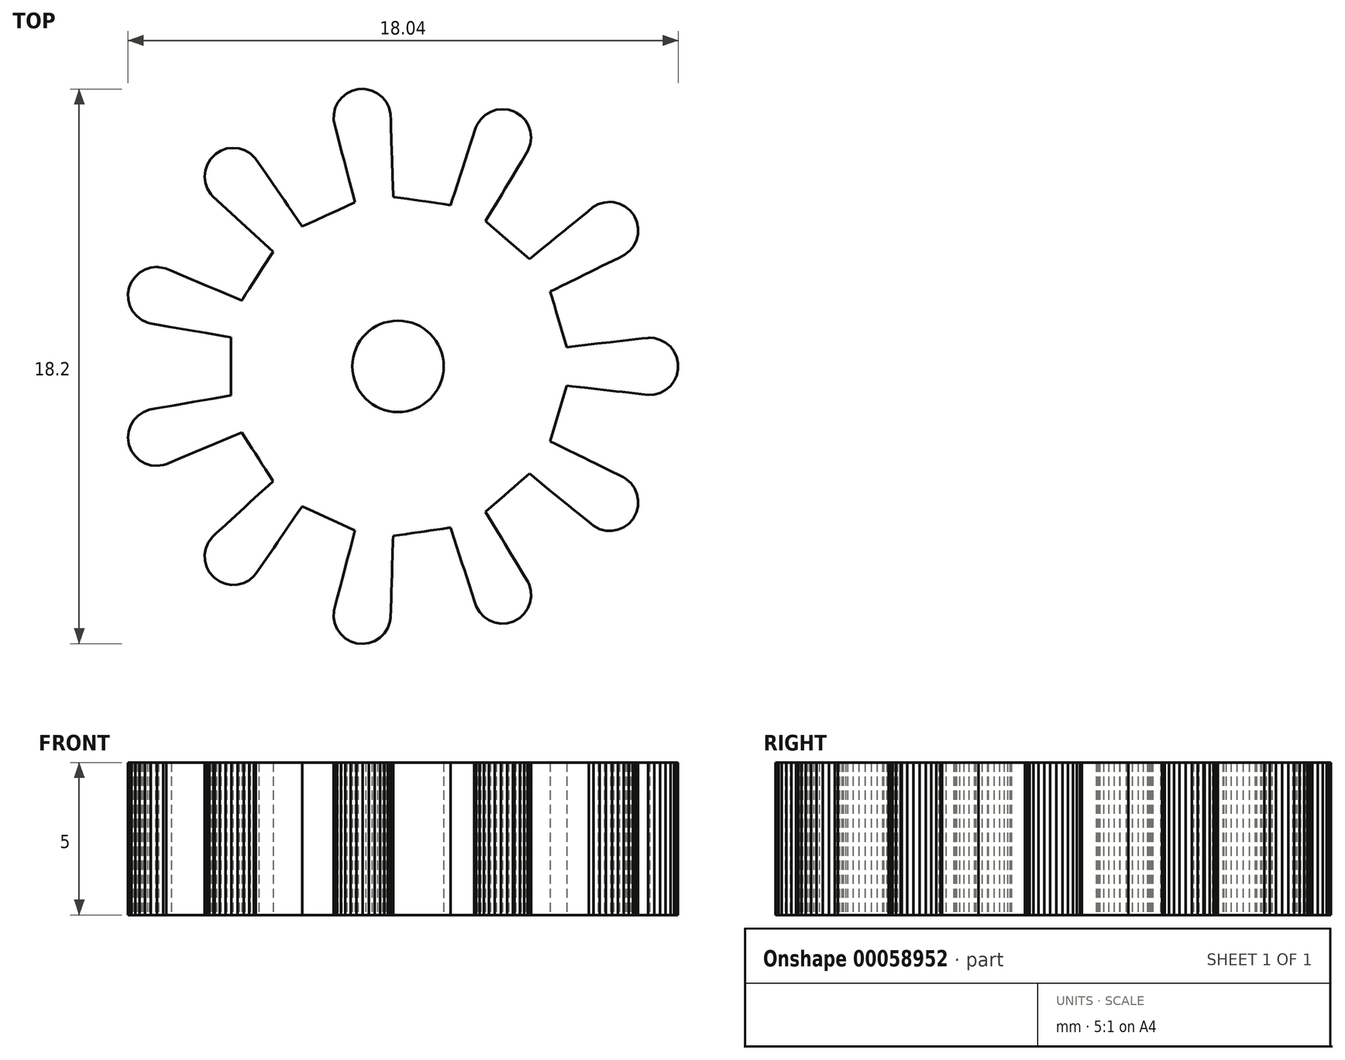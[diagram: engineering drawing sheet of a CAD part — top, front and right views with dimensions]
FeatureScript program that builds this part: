
annotation { "Feature Type Name" : "Feature", "Feature Type Description" : "" }
export const myFeature = defineFeature(function(context is Context, id is Id, definition is map)
    precondition{}
    {
        {
            var Q0;
            Q0=qCreatedBy(makeId("Top.planeOp"),FACE);
            var sketch = newSketch(context, id + "F0", { "sketchPlane" : qUnion([Q0])});
            skLineSegment(sketch, "E0", {"start": v(4.1, -0.63) * mm, "end": v(4.27, -0.65) * mm});
            skLineSegment(sketch, "E1", {"start": v(4.27, -0.65) * mm, "end": v(4.48, -0.68) * mm});
            skLineSegment(sketch, "E2", {"start": v(4.48, -0.68) * mm, "end": v(4.68, -0.7) * mm});
            skLineSegment(sketch, "E3", {"start": v(4.68, -0.7) * mm, "end": v(4.9, -0.72) * mm});
            skLineSegment(sketch, "E4", {"start": v(4.9, -0.72) * mm, "end": v(5.1, -0.75) * mm});
            skLineSegment(sketch, "E5", {"start": v(5.1, -0.75) * mm, "end": v(5.3, -0.77) * mm});
            skLineSegment(sketch, "E6", {"start": v(5.3, -0.77) * mm, "end": v(5.51, -0.8) * mm});
            skLineSegment(sketch, "E7", {"start": v(5.51, -0.8) * mm, "end": v(5.72, -0.82) * mm});
            skLineSegment(sketch, "E8", {"start": v(5.72, -0.82) * mm, "end": v(5.93, -0.84) * mm});
            skLineSegment(sketch, "E9", {"start": v(5.93, -0.84) * mm, "end": v(6.14, -0.86) * mm});
            skLineSegment(sketch, "E10", {"start": v(6.14, -0.86) * mm, "end": v(6.34, -0.89) * mm});
            skLineSegment(sketch, "E11", {"start": v(6.34, -0.89) * mm, "end": v(6.55, -0.91) * mm});
            skLineSegment(sketch, "E12", {"start": v(6.55, -0.91) * mm, "end": v(6.76, -0.94) * mm});
            skLineSegment(sketch, "E13", {"start": v(6.76, -0.94) * mm, "end": v(6.96, -0.93) * mm});
            skLineSegment(sketch, "E14", {"start": v(6.96, -0.93) * mm, "end": v(7.16, -0.87) * mm});
            skLineSegment(sketch, "E15", {"start": v(7.16, -0.87) * mm, "end": v(7.34, -0.78) * mm});
            skLineSegment(sketch, "E16", {"start": v(7.34, -0.78) * mm, "end": v(7.5, -0.65) * mm});
            skLineSegment(sketch, "E17", {"start": v(7.5, -0.65) * mm, "end": v(7.62, -0.48) * mm});
            skLineSegment(sketch, "E18", {"start": v(7.62, -0.48) * mm, "end": v(7.7, -0.3) * mm});
            skLineSegment(sketch, "E19", {"start": v(7.7, -0.3) * mm, "end": v(7.75, -0.1) * mm});
            skLineSegment(sketch, "E20", {"start": v(7.75, -0.1) * mm, "end": v(7.75, 0.1) * mm});
            skLineSegment(sketch, "E21", {"start": v(7.75, 0.1) * mm, "end": v(7.7, 0.3) * mm});
            skLineSegment(sketch, "E22", {"start": v(7.7, 0.3) * mm, "end": v(7.62, 0.48) * mm});
            skLineSegment(sketch, "E23", {"start": v(7.62, 0.48) * mm, "end": v(7.5, 0.65) * mm});
            skLineSegment(sketch, "E24", {"start": v(7.5, 0.65) * mm, "end": v(7.34, 0.78) * mm});
            skLineSegment(sketch, "E25", {"start": v(7.34, 0.78) * mm, "end": v(7.16, 0.87) * mm});
            skLineSegment(sketch, "E26", {"start": v(7.16, 0.87) * mm, "end": v(6.96, 0.93) * mm});
            skLineSegment(sketch, "E27", {"start": v(6.96, 0.93) * mm, "end": v(6.81, 0.94) * mm});
            skLineSegment(sketch, "E28", {"start": v(6.81, 0.94) * mm, "end": v(6.76, 0.94) * mm});
            skLineSegment(sketch, "E29", {"start": v(6.76, 0.94) * mm, "end": v(6.55, 0.91) * mm});
            skLineSegment(sketch, "E30", {"start": v(6.55, 0.91) * mm, "end": v(6.35, 0.89) * mm});
            skLineSegment(sketch, "E31", {"start": v(6.35, 0.89) * mm, "end": v(6.14, 0.86) * mm});
            skLineSegment(sketch, "E32", {"start": v(6.14, 0.86) * mm, "end": v(5.93, 0.84) * mm});
            skLineSegment(sketch, "E33", {"start": v(5.93, 0.84) * mm, "end": v(5.73, 0.82) * mm});
            skLineSegment(sketch, "E34", {"start": v(5.73, 0.82) * mm, "end": v(5.51, 0.8) * mm});
            skLineSegment(sketch, "E35", {"start": v(5.51, 0.8) * mm, "end": v(5.3, 0.77) * mm});
            skLineSegment(sketch, "E36", {"start": v(5.3, 0.77) * mm, "end": v(5.1, 0.75) * mm});
            skLineSegment(sketch, "E37", {"start": v(5.1, 0.75) * mm, "end": v(4.9, 0.72) * mm});
            skLineSegment(sketch, "E38", {"start": v(4.9, 0.72) * mm, "end": v(4.69, 0.7) * mm});
            skLineSegment(sketch, "E39", {"start": v(4.69, 0.7) * mm, "end": v(4.48, 0.68) * mm});
            skLineSegment(sketch, "E40", {"start": v(4.48, 0.68) * mm, "end": v(4.27, 0.65) * mm});
            skLineSegment(sketch, "E41", {"start": v(4.27, 0.65) * mm, "end": v(4.1, 0.63) * mm});
            skLineSegment(sketch, "E42", {"start": v(4.1, 0.63) * mm, "end": v(4.03, 0.83) * mm});
            skLineSegment(sketch, "E43", {"start": v(4.03, 0.83) * mm, "end": v(3.98, 1.03) * mm});
            skLineSegment(sketch, "E44", {"start": v(3.98, 1.03) * mm, "end": v(3.92, 1.23) * mm});
            skLineSegment(sketch, "E45", {"start": v(3.92, 1.23) * mm, "end": v(3.86, 1.42) * mm});
            skLineSegment(sketch, "E46", {"start": v(3.86, 1.42) * mm, "end": v(3.8, 1.62) * mm});
            skLineSegment(sketch, "E47", {"start": v(3.8, 1.62) * mm, "end": v(3.74, 1.82) * mm});
            skLineSegment(sketch, "E48", {"start": v(3.74, 1.82) * mm, "end": v(3.68, 2.02) * mm});
            skLineSegment(sketch, "E49", {"start": v(3.68, 2.02) * mm, "end": v(3.63, 2.22) * mm});
            skLineSegment(sketch, "E50", {"start": v(3.63, 2.22) * mm, "end": v(3.57, 2.41) * mm});
            skLineSegment(sketch, "E51", {"start": v(3.57, 2.41) * mm, "end": v(3.56, 2.46) * mm});
            skLineSegment(sketch, "E52", {"start": v(3.56, 2.46) * mm, "end": v(3.74, 2.55) * mm});
            skLineSegment(sketch, "E53", {"start": v(3.74, 2.55) * mm, "end": v(3.93, 2.64) * mm});
            skLineSegment(sketch, "E54", {"start": v(3.93, 2.64) * mm, "end": v(4.12, 2.73) * mm});
            skLineSegment(sketch, "E55", {"start": v(4.12, 2.73) * mm, "end": v(4.3, 2.83) * mm});
            skLineSegment(sketch, "E56", {"start": v(4.3, 2.83) * mm, "end": v(4.49, 2.92) * mm});
            skLineSegment(sketch, "E57", {"start": v(4.49, 2.92) * mm, "end": v(4.68, 3.01) * mm});
            skLineSegment(sketch, "E58", {"start": v(4.68, 3.01) * mm, "end": v(4.87, 3.1) * mm});
            skLineSegment(sketch, "E59", {"start": v(4.87, 3.1) * mm, "end": v(5.05, 3.2) * mm});
            skLineSegment(sketch, "E60", {"start": v(5.05, 3.2) * mm, "end": v(5.24, 3.29) * mm});
            skLineSegment(sketch, "E61", {"start": v(5.24, 3.29) * mm, "end": v(5.43, 3.38) * mm});
            skLineSegment(sketch, "E62", {"start": v(5.43, 3.38) * mm, "end": v(5.61, 3.47) * mm});
            skLineSegment(sketch, "E63", {"start": v(5.61, 3.47) * mm, "end": v(5.8, 3.57) * mm});
            skLineSegment(sketch, "E64", {"start": v(5.8, 3.57) * mm, "end": v(5.99, 3.66) * mm});
            skLineSegment(sketch, "E65", {"start": v(5.99, 3.66) * mm, "end": v(6.17, 3.8) * mm});
            skLineSegment(sketch, "E66", {"start": v(6.17, 3.8) * mm, "end": v(6.3, 3.96) * mm});
            skLineSegment(sketch, "E67", {"start": v(6.3, 3.96) * mm, "end": v(6.38, 4.14) * mm});
            skLineSegment(sketch, "E68", {"start": v(6.38, 4.14) * mm, "end": v(6.43, 4.33) * mm});
            skLineSegment(sketch, "E69", {"start": v(6.43, 4.33) * mm, "end": v(6.44, 4.54) * mm});
            skLineSegment(sketch, "E70", {"start": v(6.44, 4.54) * mm, "end": v(6.4, 4.74) * mm});
            skLineSegment(sketch, "E71", {"start": v(6.4, 4.74) * mm, "end": v(6.32, 4.92) * mm});
            skLineSegment(sketch, "E72", {"start": v(6.32, 4.92) * mm, "end": v(6.3, 4.97) * mm});
            skLineSegment(sketch, "E73", {"start": v(6.3, 4.97) * mm, "end": v(6.16, 5.13) * mm});
            skLineSegment(sketch, "E74", {"start": v(6.16, 5.13) * mm, "end": v(6, 5.25) * mm});
            skLineSegment(sketch, "E75", {"start": v(6, 5.25) * mm, "end": v(5.82, 5.34) * mm});
            skLineSegment(sketch, "E76", {"start": v(5.82, 5.34) * mm, "end": v(5.63, 5.39) * mm});
            skLineSegment(sketch, "E77", {"start": v(5.63, 5.39) * mm, "end": v(5.53, 5.4) * mm});
            skLineSegment(sketch, "E78", {"start": v(5.53, 5.4) * mm, "end": v(5.32, 5.38) * mm});
            skLineSegment(sketch, "E79", {"start": v(5.32, 5.38) * mm, "end": v(5.13, 5.32) * mm});
            skLineSegment(sketch, "E80", {"start": v(5.13, 5.32) * mm, "end": v(4.95, 5.22) * mm});
            skLineSegment(sketch, "E81", {"start": v(4.95, 5.22) * mm, "end": v(4.8, 5.09) * mm});
            skLineSegment(sketch, "E82", {"start": v(4.8, 5.09) * mm, "end": v(4.63, 4.96) * mm});
            skLineSegment(sketch, "E83", {"start": v(4.63, 4.96) * mm, "end": v(4.47, 4.82) * mm});
            skLineSegment(sketch, "E84", {"start": v(4.47, 4.82) * mm, "end": v(4.3, 4.7) * mm});
            skLineSegment(sketch, "E85", {"start": v(4.3, 4.7) * mm, "end": v(4.15, 4.56) * mm});
            skLineSegment(sketch, "E86", {"start": v(4.15, 4.56) * mm, "end": v(3.98, 4.43) * mm});
            skLineSegment(sketch, "E87", {"start": v(3.98, 4.43) * mm, "end": v(3.82, 4.3) * mm});
            skLineSegment(sketch, "E88", {"start": v(3.82, 4.3) * mm, "end": v(3.66, 4.16) * mm});
            skLineSegment(sketch, "E89", {"start": v(3.66, 4.16) * mm, "end": v(3.5, 4.03) * mm});
            skLineSegment(sketch, "E90", {"start": v(3.5, 4.03) * mm, "end": v(3.34, 3.9) * mm});
            skLineSegment(sketch, "E91", {"start": v(3.34, 3.9) * mm, "end": v(3.18, 3.77) * mm});
            skLineSegment(sketch, "E92", {"start": v(3.18, 3.77) * mm, "end": v(3.01, 3.63) * mm});
            skLineSegment(sketch, "E93", {"start": v(3.01, 3.63) * mm, "end": v(2.87, 3.52) * mm});
            skLineSegment(sketch, "E94", {"start": v(2.87, 3.52) * mm, "end": v(2.72, 3.66) * mm});
            skLineSegment(sketch, "E95", {"start": v(2.72, 3.66) * mm, "end": v(2.56, 3.8) * mm});
            skLineSegment(sketch, "E96", {"start": v(2.56, 3.8) * mm, "end": v(2.4, 3.93) * mm});
            skLineSegment(sketch, "E97", {"start": v(2.4, 3.93) * mm, "end": v(2.25, 4.06) * mm});
            skLineSegment(sketch, "E98", {"start": v(2.25, 4.06) * mm, "end": v(2.1, 4.2) * mm});
            skLineSegment(sketch, "E99", {"start": v(2.1, 4.2) * mm, "end": v(1.94, 4.33) * mm});
            skLineSegment(sketch, "E100", {"start": v(1.94, 4.33) * mm, "end": v(1.78, 4.47) * mm});
            skLineSegment(sketch, "E101", {"start": v(1.78, 4.47) * mm, "end": v(1.62, 4.6) * mm});
            skLineSegment(sketch, "E102", {"start": v(1.62, 4.6) * mm, "end": v(1.47, 4.74) * mm});
            skLineSegment(sketch, "E103", {"start": v(1.47, 4.74) * mm, "end": v(1.43, 4.77) * mm});
            skLineSegment(sketch, "E104", {"start": v(1.43, 4.77) * mm, "end": v(1.54, 4.94) * mm});
            skLineSegment(sketch, "E105", {"start": v(1.54, 4.94) * mm, "end": v(1.65, 5.12) * mm});
            skLineSegment(sketch, "E106", {"start": v(1.65, 5.12) * mm, "end": v(1.76, 5.3) * mm});
            skLineSegment(sketch, "E107", {"start": v(1.76, 5.3) * mm, "end": v(1.86, 5.48) * mm});
            skLineSegment(sketch, "E108", {"start": v(1.86, 5.48) * mm, "end": v(1.97, 5.66) * mm});
            skLineSegment(sketch, "E109", {"start": v(1.97, 5.66) * mm, "end": v(2.08, 5.84) * mm});
            skLineSegment(sketch, "E110", {"start": v(2.08, 5.84) * mm, "end": v(2.19, 6.02) * mm});
            skLineSegment(sketch, "E111", {"start": v(2.19, 6.02) * mm, "end": v(2.3, 6.2) * mm});
            skLineSegment(sketch, "E112", {"start": v(2.3, 6.2) * mm, "end": v(2.4, 6.38) * mm});
            skLineSegment(sketch, "E113", {"start": v(2.4, 6.38) * mm, "end": v(2.51, 6.55) * mm});
            skLineSegment(sketch, "E114", {"start": v(2.51, 6.55) * mm, "end": v(2.62, 6.73) * mm});
            skLineSegment(sketch, "E115", {"start": v(2.62, 6.73) * mm, "end": v(2.73, 6.91) * mm});
            skLineSegment(sketch, "E116", {"start": v(2.73, 6.91) * mm, "end": v(2.83, 7.1) * mm});
            skLineSegment(sketch, "E117", {"start": v(2.83, 7.1) * mm, "end": v(2.9, 7.3) * mm});
            skLineSegment(sketch, "E118", {"start": v(2.9, 7.3) * mm, "end": v(2.93, 7.5) * mm});
            skLineSegment(sketch, "E119", {"start": v(2.93, 7.5) * mm, "end": v(2.9, 7.7) * mm});
            skLineSegment(sketch, "E120", {"start": v(2.9, 7.7) * mm, "end": v(2.84, 7.9) * mm});
            skLineSegment(sketch, "E121", {"start": v(2.84, 7.9) * mm, "end": v(2.73, 8.07) * mm});
            skLineSegment(sketch, "E122", {"start": v(2.73, 8.07) * mm, "end": v(2.6, 8.22) * mm});
            skLineSegment(sketch, "E123", {"start": v(2.6, 8.22) * mm, "end": v(2.43, 8.33) * mm});
            skLineSegment(sketch, "E124", {"start": v(2.43, 8.33) * mm, "end": v(2.38, 8.36) * mm});
            skLineSegment(sketch, "E125", {"start": v(2.38, 8.36) * mm, "end": v(2.19, 8.42) * mm});
            skLineSegment(sketch, "E126", {"start": v(2.19, 8.42) * mm, "end": v(1.99, 8.44) * mm});
            skLineSegment(sketch, "E127", {"start": v(1.99, 8.44) * mm, "end": v(1.78, 8.42) * mm});
            skLineSegment(sketch, "E128", {"start": v(1.78, 8.42) * mm, "end": v(1.6, 8.35) * mm});
            skLineSegment(sketch, "E129", {"start": v(1.6, 8.35) * mm, "end": v(1.42, 8.25) * mm});
            skLineSegment(sketch, "E130", {"start": v(1.42, 8.25) * mm, "end": v(1.27, 8.1) * mm});
            skLineSegment(sketch, "E131", {"start": v(1.27, 8.1) * mm, "end": v(1.16, 7.94) * mm});
            skLineSegment(sketch, "E132", {"start": v(1.16, 7.94) * mm, "end": v(1.12, 7.84) * mm});
            skLineSegment(sketch, "E133", {"start": v(1.12, 7.84) * mm, "end": v(1.05, 7.65) * mm});
            skLineSegment(sketch, "E134", {"start": v(1.05, 7.65) * mm, "end": v(0.99, 7.45) * mm});
            skLineSegment(sketch, "E135", {"start": v(0.99, 7.45) * mm, "end": v(0.92, 7.25) * mm});
            skLineSegment(sketch, "E136", {"start": v(0.92, 7.25) * mm, "end": v(0.86, 7.05) * mm});
            skLineSegment(sketch, "E137", {"start": v(0.86, 7.05) * mm, "end": v(0.8, 6.86) * mm});
            skLineSegment(sketch, "E138", {"start": v(0.8, 6.86) * mm, "end": v(0.73, 6.65) * mm});
            skLineSegment(sketch, "E139", {"start": v(0.73, 6.65) * mm, "end": v(0.67, 6.46) * mm});
            skLineSegment(sketch, "E140", {"start": v(0.67, 6.46) * mm, "end": v(0.6, 6.26) * mm});
            skLineSegment(sketch, "E141", {"start": v(0.6, 6.26) * mm, "end": v(0.54, 6.06) * mm});
            skLineSegment(sketch, "E142", {"start": v(0.54, 6.06) * mm, "end": v(0.47, 5.86) * mm});
            skLineSegment(sketch, "E143", {"start": v(0.47, 5.86) * mm, "end": v(0.4, 5.66) * mm});
            skLineSegment(sketch, "E144", {"start": v(0.4, 5.66) * mm, "end": v(0.34, 5.46) * mm});
            skLineSegment(sketch, "E145", {"start": v(0.34, 5.46) * mm, "end": v(0.29, 5.3) * mm});
            skLineSegment(sketch, "E146", {"start": v(0.29, 5.3) * mm, "end": v(0.08, 5.32) * mm});
            skLineSegment(sketch, "E147", {"start": v(0.08, 5.32) * mm, "end": v(-0.12, 5.35) * mm});
            skLineSegment(sketch, "E148", {"start": v(-0.12, 5.35) * mm, "end": v(-0.33, 5.38) * mm});
            skLineSegment(sketch, "E149", {"start": v(-0.33, 5.38) * mm, "end": v(-0.53, 5.4) * mm});
            skLineSegment(sketch, "E150", {"start": v(-0.53, 5.4) * mm, "end": v(-0.74, 5.44) * mm});
            skLineSegment(sketch, "E151", {"start": v(-0.74, 5.44) * mm, "end": v(-0.94, 5.47) * mm});
            skLineSegment(sketch, "E152", {"start": v(-0.94, 5.47) * mm, "end": v(-1.15, 5.5) * mm});
            skLineSegment(sketch, "E153", {"start": v(-1.15, 5.5) * mm, "end": v(-1.35, 5.53) * mm});
            skLineSegment(sketch, "E154", {"start": v(-1.35, 5.53) * mm, "end": v(-1.55, 5.56) * mm});
            skLineSegment(sketch, "E155", {"start": v(-1.55, 5.56) * mm, "end": v(-1.6, 5.56) * mm});
            skLineSegment(sketch, "E156", {"start": v(-1.6, 5.56) * mm, "end": v(-1.6, 5.77) * mm});
            skLineSegment(sketch, "E157", {"start": v(-1.6, 5.77) * mm, "end": v(-1.61, 5.98) * mm});
            skLineSegment(sketch, "E158", {"start": v(-1.61, 5.98) * mm, "end": v(-1.62, 6.19) * mm});
            skLineSegment(sketch, "E159", {"start": v(-1.62, 6.19) * mm, "end": v(-1.62, 6.4) * mm});
            skLineSegment(sketch, "E160", {"start": v(-1.62, 6.4) * mm, "end": v(-1.63, 6.6) * mm});
            skLineSegment(sketch, "E161", {"start": v(-1.63, 6.6) * mm, "end": v(-1.64, 6.82) * mm});
            skLineSegment(sketch, "E162", {"start": v(-1.64, 6.82) * mm, "end": v(-1.64, 7.02) * mm});
            skLineSegment(sketch, "E163", {"start": v(-1.64, 7.02) * mm, "end": v(-1.65, 7.23) * mm});
            skLineSegment(sketch, "E164", {"start": v(-1.65, 7.23) * mm, "end": v(-1.65, 7.44) * mm});
            skLineSegment(sketch, "E165", {"start": v(-1.65, 7.44) * mm, "end": v(-1.66, 7.65) * mm});
            skLineSegment(sketch, "E166", {"start": v(-1.66, 7.65) * mm, "end": v(-1.67, 7.85) * mm});
            skLineSegment(sketch, "E167", {"start": v(-1.67, 7.85) * mm, "end": v(-1.67, 8.07) * mm});
            skLineSegment(sketch, "E168", {"start": v(-1.67, 8.07) * mm, "end": v(-1.68, 8.27) * mm});
            skLineSegment(sketch, "E169", {"start": v(-1.68, 8.27) * mm, "end": v(-1.73, 8.5) * mm});
            skLineSegment(sketch, "E170", {"start": v(-1.73, 8.5) * mm, "end": v(-1.82, 8.68) * mm});
            skLineSegment(sketch, "E171", {"start": v(-1.82, 8.68) * mm, "end": v(-1.95, 8.83) * mm});
            skLineSegment(sketch, "E172", {"start": v(-1.95, 8.83) * mm, "end": v(-2.11, 8.96) * mm});
            skLineSegment(sketch, "E173", {"start": v(-2.11, 8.96) * mm, "end": v(-2.3, 9.05) * mm});
            skLineSegment(sketch, "E174", {"start": v(-2.3, 9.05) * mm, "end": v(-2.5, 9.1) * mm});
            skLineSegment(sketch, "E175", {"start": v(-2.5, 9.1) * mm, "end": v(-2.6, 9.1) * mm});
            skLineSegment(sketch, "E176", {"start": v(-2.6, 9.1) * mm, "end": v(-2.74, 9.1) * mm});
            skLineSegment(sketch, "E177", {"start": v(-2.74, 9.1) * mm, "end": v(-2.94, 9.04) * mm});
            skLineSegment(sketch, "E178", {"start": v(-2.94, 9.04) * mm, "end": v(-3.12, 8.95) * mm});
            skLineSegment(sketch, "E179", {"start": v(-3.12, 8.95) * mm, "end": v(-3.28, 8.82) * mm});
            skLineSegment(sketch, "E180", {"start": v(-3.28, 8.82) * mm, "end": v(-3.4, 8.66) * mm});
            skLineSegment(sketch, "E181", {"start": v(-3.4, 8.66) * mm, "end": v(-3.5, 8.48) * mm});
            skLineSegment(sketch, "E182", {"start": v(-3.5, 8.48) * mm, "end": v(-3.54, 8.28) * mm});
            skLineSegment(sketch, "E183", {"start": v(-3.54, 8.28) * mm, "end": v(-3.54, 8.08) * mm});
            skLineSegment(sketch, "E184", {"start": v(-3.54, 8.08) * mm, "end": v(-3.53, 7.98) * mm});
            skLineSegment(sketch, "E185", {"start": v(-3.53, 7.98) * mm, "end": v(-3.48, 7.78) * mm});
            skLineSegment(sketch, "E186", {"start": v(-3.48, 7.78) * mm, "end": v(-3.42, 7.58) * mm});
            skLineSegment(sketch, "E187", {"start": v(-3.42, 7.58) * mm, "end": v(-3.37, 7.37) * mm});
            skLineSegment(sketch, "E188", {"start": v(-3.37, 7.37) * mm, "end": v(-3.32, 7.17) * mm});
            skLineSegment(sketch, "E189", {"start": v(-3.32, 7.17) * mm, "end": v(-3.27, 6.97) * mm});
            skLineSegment(sketch, "E190", {"start": v(-3.27, 6.97) * mm, "end": v(-3.21, 6.77) * mm});
            skLineSegment(sketch, "E191", {"start": v(-3.21, 6.77) * mm, "end": v(-3.16, 6.57) * mm});
            skLineSegment(sketch, "E192", {"start": v(-3.16, 6.57) * mm, "end": v(-3.1, 6.37) * mm});
            skLineSegment(sketch, "E193", {"start": v(-3.1, 6.37) * mm, "end": v(-3.05, 6.16) * mm});
            skLineSegment(sketch, "E194", {"start": v(-3.05, 6.16) * mm, "end": v(-3, 5.96) * mm});
            skLineSegment(sketch, "E195", {"start": v(-3, 5.96) * mm, "end": v(-2.95, 5.76) * mm});
            skLineSegment(sketch, "E196", {"start": v(-2.95, 5.76) * mm, "end": v(-2.9, 5.56) * mm});
            skLineSegment(sketch, "E197", {"start": v(-2.9, 5.56) * mm, "end": v(-2.85, 5.38) * mm});
            skLineSegment(sketch, "E198", {"start": v(-2.85, 5.38) * mm, "end": v(-3.04, 5.3) * mm});
            skLineSegment(sketch, "E199", {"start": v(-3.04, 5.3) * mm, "end": v(-3.22, 5.21) * mm});
            skLineSegment(sketch, "E200", {"start": v(-3.22, 5.21) * mm, "end": v(-3.41, 5.13) * mm});
            skLineSegment(sketch, "E201", {"start": v(-3.41, 5.13) * mm, "end": v(-3.6, 5.04) * mm});
            skLineSegment(sketch, "E202", {"start": v(-3.6, 5.04) * mm, "end": v(-3.79, 4.95) * mm});
            skLineSegment(sketch, "E203", {"start": v(-3.79, 4.95) * mm, "end": v(-3.98, 4.87) * mm});
            skLineSegment(sketch, "E204", {"start": v(-3.98, 4.87) * mm, "end": v(-4.16, 4.78) * mm});
            skLineSegment(sketch, "E205", {"start": v(-4.16, 4.78) * mm, "end": v(-4.35, 4.7) * mm});
            skLineSegment(sketch, "E206", {"start": v(-4.35, 4.7) * mm, "end": v(-4.54, 4.61) * mm});
            skLineSegment(sketch, "E207", {"start": v(-4.54, 4.61) * mm, "end": v(-4.58, 4.6) * mm});
            skLineSegment(sketch, "E208", {"start": v(-4.58, 4.6) * mm, "end": v(-4.7, 4.76) * mm});
            skLineSegment(sketch, "E209", {"start": v(-4.7, 4.76) * mm, "end": v(-4.81, 4.93) * mm});
            skLineSegment(sketch, "E210", {"start": v(-4.81, 4.93) * mm, "end": v(-4.93, 5.1) * mm});
            skLineSegment(sketch, "E211", {"start": v(-4.93, 5.1) * mm, "end": v(-5.05, 5.28) * mm});
            skLineSegment(sketch, "E212", {"start": v(-5.05, 5.28) * mm, "end": v(-5.17, 5.45) * mm});
            skLineSegment(sketch, "E213", {"start": v(-5.17, 5.45) * mm, "end": v(-5.29, 5.63) * mm});
            skLineSegment(sketch, "E214", {"start": v(-5.29, 5.63) * mm, "end": v(-5.4, 5.8) * mm});
            skLineSegment(sketch, "E215", {"start": v(-5.4, 5.8) * mm, "end": v(-5.52, 5.97) * mm});
            skLineSegment(sketch, "E216", {"start": v(-5.52, 5.97) * mm, "end": v(-5.64, 6.14) * mm});
            skLineSegment(sketch, "E217", {"start": v(-5.64, 6.14) * mm, "end": v(-5.76, 6.31) * mm});
            skLineSegment(sketch, "E218", {"start": v(-5.76, 6.31) * mm, "end": v(-5.88, 6.48) * mm});
            skLineSegment(sketch, "E219", {"start": v(-5.88, 6.48) * mm, "end": v(-6, 6.66) * mm});
            skLineSegment(sketch, "E220", {"start": v(-6, 6.66) * mm, "end": v(-6.12, 6.83) * mm});
            skLineSegment(sketch, "E221", {"start": v(-6.12, 6.83) * mm, "end": v(-6.28, 6.99) * mm});
            skLineSegment(sketch, "E222", {"start": v(-6.28, 6.99) * mm, "end": v(-6.45, 7.09) * mm});
            skLineSegment(sketch, "E223", {"start": v(-6.45, 7.09) * mm, "end": v(-6.65, 7.15) * mm});
            skLineSegment(sketch, "E224", {"start": v(-6.65, 7.15) * mm, "end": v(-6.85, 7.17) * mm});
            skLineSegment(sketch, "E225", {"start": v(-6.85, 7.17) * mm, "end": v(-7.05, 7.15) * mm});
            skLineSegment(sketch, "E226", {"start": v(-7.05, 7.15) * mm, "end": v(-7.24, 7.08) * mm});
            skLineSegment(sketch, "E227", {"start": v(-7.24, 7.08) * mm, "end": v(-7.41, 6.98) * mm});
            skLineSegment(sketch, "E228", {"start": v(-7.41, 6.98) * mm, "end": v(-7.45, 6.94) * mm});
            skLineSegment(sketch, "E229", {"start": v(-7.45, 6.94) * mm, "end": v(-7.6, 6.8) * mm});
            skLineSegment(sketch, "E230", {"start": v(-7.6, 6.8) * mm, "end": v(-7.7, 6.62) * mm});
            skLineSegment(sketch, "E231", {"start": v(-7.7, 6.62) * mm, "end": v(-7.76, 6.43) * mm});
            skLineSegment(sketch, "E232", {"start": v(-7.76, 6.43) * mm, "end": v(-7.78, 6.22) * mm});
            skLineSegment(sketch, "E233", {"start": v(-7.78, 6.22) * mm, "end": v(-7.75, 6.02) * mm});
            skLineSegment(sketch, "E234", {"start": v(-7.75, 6.02) * mm, "end": v(-7.69, 5.83) * mm});
            skLineSegment(sketch, "E235", {"start": v(-7.69, 5.83) * mm, "end": v(-7.58, 5.66) * mm});
            skLineSegment(sketch, "E236", {"start": v(-7.58, 5.66) * mm, "end": v(-7.51, 5.58) * mm});
            skLineSegment(sketch, "E237", {"start": v(-7.51, 5.58) * mm, "end": v(-7.36, 5.44) * mm});
            skLineSegment(sketch, "E238", {"start": v(-7.36, 5.44) * mm, "end": v(-7.2, 5.3) * mm});
            skLineSegment(sketch, "E239", {"start": v(-7.2, 5.3) * mm, "end": v(-7.05, 5.16) * mm});
            skLineSegment(sketch, "E240", {"start": v(-7.05, 5.16) * mm, "end": v(-6.9, 5.02) * mm});
            skLineSegment(sketch, "E241", {"start": v(-6.9, 5.02) * mm, "end": v(-6.75, 4.88) * mm});
            skLineSegment(sketch, "E242", {"start": v(-6.75, 4.88) * mm, "end": v(-6.59, 4.73) * mm});
            skLineSegment(sketch, "E243", {"start": v(-6.59, 4.73) * mm, "end": v(-6.44, 4.6) * mm});
            skLineSegment(sketch, "E244", {"start": v(-6.44, 4.6) * mm, "end": v(-6.28, 4.45) * mm});
            skLineSegment(sketch, "E245", {"start": v(-6.28, 4.45) * mm, "end": v(-6.13, 4.31) * mm});
            skLineSegment(sketch, "E246", {"start": v(-6.13, 4.31) * mm, "end": v(-5.98, 4.17) * mm});
            skLineSegment(sketch, "E247", {"start": v(-5.98, 4.17) * mm, "end": v(-5.82, 4.03) * mm});
            skLineSegment(sketch, "E248", {"start": v(-5.82, 4.03) * mm, "end": v(-5.67, 3.89) * mm});
            skLineSegment(sketch, "E249", {"start": v(-5.67, 3.89) * mm, "end": v(-5.53, 3.77) * mm});
            skLineSegment(sketch, "E250", {"start": v(-5.53, 3.77) * mm, "end": v(-5.65, 3.6) * mm});
            skLineSegment(sketch, "E251", {"start": v(-5.65, 3.6) * mm, "end": v(-5.76, 3.42) * mm});
            skLineSegment(sketch, "E252", {"start": v(-5.76, 3.42) * mm, "end": v(-5.87, 3.24) * mm});
            skLineSegment(sketch, "E253", {"start": v(-5.87, 3.24) * mm, "end": v(-5.98, 3.07) * mm});
            skLineSegment(sketch, "E254", {"start": v(-5.98, 3.07) * mm, "end": v(-6.1, 2.9) * mm});
            skLineSegment(sketch, "E255", {"start": v(-6.1, 2.9) * mm, "end": v(-6.2, 2.72) * mm});
            skLineSegment(sketch, "E256", {"start": v(-6.2, 2.72) * mm, "end": v(-6.32, 2.55) * mm});
            skLineSegment(sketch, "E257", {"start": v(-6.32, 2.55) * mm, "end": v(-6.43, 2.38) * mm});
            skLineSegment(sketch, "E258", {"start": v(-6.43, 2.38) * mm, "end": v(-6.54, 2.2) * mm});
            skLineSegment(sketch, "E259", {"start": v(-6.54, 2.2) * mm, "end": v(-6.56, 2.16) * mm});
            skLineSegment(sketch, "E260", {"start": v(-6.56, 2.16) * mm, "end": v(-6.75, 2.24) * mm});
            skLineSegment(sketch, "E261", {"start": v(-6.75, 2.24) * mm, "end": v(-6.94, 2.32) * mm});
            skLineSegment(sketch, "E262", {"start": v(-6.94, 2.32) * mm, "end": v(-7.14, 2.4) * mm});
            skLineSegment(sketch, "E263", {"start": v(-7.14, 2.4) * mm, "end": v(-7.33, 2.49) * mm});
            skLineSegment(sketch, "E264", {"start": v(-7.33, 2.49) * mm, "end": v(-7.52, 2.57) * mm});
            skLineSegment(sketch, "E265", {"start": v(-7.52, 2.57) * mm, "end": v(-7.72, 2.65) * mm});
            skLineSegment(sketch, "E266", {"start": v(-7.72, 2.65) * mm, "end": v(-7.9, 2.73) * mm});
            skLineSegment(sketch, "E267", {"start": v(-7.9, 2.73) * mm, "end": v(-8.1, 2.81) * mm});
            skLineSegment(sketch, "E268", {"start": v(-8.1, 2.81) * mm, "end": v(-8.3, 2.9) * mm});
            skLineSegment(sketch, "E269", {"start": v(-8.3, 2.9) * mm, "end": v(-8.49, 2.97) * mm});
            skLineSegment(sketch, "E270", {"start": v(-8.49, 2.97) * mm, "end": v(-8.68, 3.05) * mm});
            skLineSegment(sketch, "E271", {"start": v(-8.68, 3.05) * mm, "end": v(-8.87, 3.14) * mm});
            skLineSegment(sketch, "E272", {"start": v(-8.87, 3.14) * mm, "end": v(-9.06, 3.21) * mm});
            skLineSegment(sketch, "E273", {"start": v(-9.06, 3.21) * mm, "end": v(-9.29, 3.26) * mm});
            skLineSegment(sketch, "E274", {"start": v(-9.29, 3.26) * mm, "end": v(-9.34, 3.26) * mm});
            skLineSegment(sketch, "E275", {"start": v(-9.34, 3.26) * mm, "end": v(-9.54, 3.24) * mm});
            skLineSegment(sketch, "E276", {"start": v(-9.54, 3.24) * mm, "end": v(-9.73, 3.18) * mm});
            skLineSegment(sketch, "E277", {"start": v(-9.73, 3.18) * mm, "end": v(-9.9, 3.08) * mm});
            skLineSegment(sketch, "E278", {"start": v(-9.9, 3.08) * mm, "end": v(-10.06, 2.94) * mm});
            skLineSegment(sketch, "E279", {"start": v(-10.06, 2.94) * mm, "end": v(-10.17, 2.78) * mm});
            skLineSegment(sketch, "E280", {"start": v(-10.17, 2.78) * mm, "end": v(-10.25, 2.59) * mm});
            skLineSegment(sketch, "E281", {"start": v(-10.25, 2.59) * mm, "end": v(-10.29, 2.39) * mm});
            skLineSegment(sketch, "E282", {"start": v(-10.29, 2.39) * mm, "end": v(-10.28, 2.19) * mm});
            skLineSegment(sketch, "E283", {"start": v(-10.28, 2.19) * mm, "end": v(-10.23, 1.99) * mm});
            skLineSegment(sketch, "E284", {"start": v(-10.23, 1.99) * mm, "end": v(-10.14, 1.8) * mm});
            skLineSegment(sketch, "E285", {"start": v(-10.14, 1.8) * mm, "end": v(-10, 1.65) * mm});
            skLineSegment(sketch, "E286", {"start": v(-10, 1.65) * mm, "end": v(-9.85, 1.53) * mm});
            skLineSegment(sketch, "E287", {"start": v(-9.85, 1.53) * mm, "end": v(-9.66, 1.44) * mm});
            skLineSegment(sketch, "E288", {"start": v(-9.66, 1.44) * mm, "end": v(-9.57, 1.41) * mm});
            skLineSegment(sketch, "E289", {"start": v(-9.57, 1.41) * mm, "end": v(-9.36, 1.38) * mm});
            skLineSegment(sketch, "E290", {"start": v(-9.36, 1.38) * mm, "end": v(-9.16, 1.34) * mm});
            skLineSegment(sketch, "E291", {"start": v(-9.16, 1.34) * mm, "end": v(-8.95, 1.3) * mm});
            skLineSegment(sketch, "E292", {"start": v(-8.95, 1.3) * mm, "end": v(-8.74, 1.27) * mm});
            skLineSegment(sketch, "E293", {"start": v(-8.74, 1.27) * mm, "end": v(-8.54, 1.23) * mm});
            skLineSegment(sketch, "E294", {"start": v(-8.54, 1.23) * mm, "end": v(-8.33, 1.2) * mm});
            skLineSegment(sketch, "E295", {"start": v(-8.33, 1.2) * mm, "end": v(-8.13, 1.16) * mm});
            skLineSegment(sketch, "E296", {"start": v(-8.13, 1.16) * mm, "end": v(-7.92, 1.13) * mm});
            skLineSegment(sketch, "E297", {"start": v(-7.92, 1.13) * mm, "end": v(-7.71, 1.09) * mm});
            skLineSegment(sketch, "E298", {"start": v(-7.71, 1.09) * mm, "end": v(-7.5, 1.05) * mm});
            skLineSegment(sketch, "E299", {"start": v(-7.5, 1.05) * mm, "end": v(-7.3, 1.02) * mm});
            skLineSegment(sketch, "E300", {"start": v(-7.3, 1.02) * mm, "end": v(-7.1, 0.98) * mm});
            skLineSegment(sketch, "E301", {"start": v(-7.1, 0.98) * mm, "end": v(-6.92, 0.95) * mm});
            skLineSegment(sketch, "E302", {"start": v(-6.92, 0.95) * mm, "end": v(-6.92, 0.75) * mm});
            skLineSegment(sketch, "E303", {"start": v(-6.92, 0.75) * mm, "end": v(-6.92, 0.54) * mm});
            skLineSegment(sketch, "E304", {"start": v(-6.92, 0.54) * mm, "end": v(-6.92, 0.33) * mm});
            skLineSegment(sketch, "E305", {"start": v(-6.92, 0.33) * mm, "end": v(-6.92, 0.13) * mm});
            skLineSegment(sketch, "E306", {"start": v(-6.92, 0.13) * mm, "end": v(-6.92, -0.08) * mm});
            skLineSegment(sketch, "E307", {"start": v(-6.92, -0.08) * mm, "end": v(-6.92, -0.29) * mm});
            skLineSegment(sketch, "E308", {"start": v(-6.92, -0.29) * mm, "end": v(-6.92, -0.5) * mm});
            skLineSegment(sketch, "E309", {"start": v(-6.92, -0.5) * mm, "end": v(-6.92, -0.7) * mm});
            skLineSegment(sketch, "E310", {"start": v(-6.92, -0.7) * mm, "end": v(-6.92, -0.9) * mm});
            skLineSegment(sketch, "E311", {"start": v(-6.92, -0.9) * mm, "end": v(-6.92, -0.95) * mm});
            skLineSegment(sketch, "E312", {"start": v(-6.92, -0.95) * mm, "end": v(-7.12, -0.99) * mm});
            skLineSegment(sketch, "E313", {"start": v(-7.12, -0.99) * mm, "end": v(-7.33, -1.02) * mm});
            skLineSegment(sketch, "E314", {"start": v(-7.33, -1.02) * mm, "end": v(-7.54, -1.06) * mm});
            skLineSegment(sketch, "E315", {"start": v(-7.54, -1.06) * mm, "end": v(-7.74, -1.1) * mm});
            skLineSegment(sketch, "E316", {"start": v(-7.74, -1.1) * mm, "end": v(-7.94, -1.13) * mm});
            skLineSegment(sketch, "E317", {"start": v(-7.94, -1.13) * mm, "end": v(-8.15, -1.17) * mm});
            skLineSegment(sketch, "E318", {"start": v(-8.15, -1.17) * mm, "end": v(-8.36, -1.2) * mm});
            skLineSegment(sketch, "E319", {"start": v(-8.36, -1.2) * mm, "end": v(-8.56, -1.24) * mm});
            skLineSegment(sketch, "E320", {"start": v(-8.56, -1.24) * mm, "end": v(-8.77, -1.27) * mm});
            skLineSegment(sketch, "E321", {"start": v(-8.77, -1.27) * mm, "end": v(-8.97, -1.3) * mm});
            skLineSegment(sketch, "E322", {"start": v(-8.97, -1.3) * mm, "end": v(-9.18, -1.34) * mm});
            skLineSegment(sketch, "E323", {"start": v(-9.18, -1.34) * mm, "end": v(-9.39, -1.38) * mm});
            skLineSegment(sketch, "E324", {"start": v(-9.39, -1.38) * mm, "end": v(-9.6, -1.42) * mm});
            skLineSegment(sketch, "E325", {"start": v(-9.6, -1.42) * mm, "end": v(-9.8, -1.5) * mm});
            skLineSegment(sketch, "E326", {"start": v(-9.8, -1.5) * mm, "end": v(-9.97, -1.62) * mm});
            skLineSegment(sketch, "E327", {"start": v(-9.97, -1.62) * mm, "end": v(-10.1, -1.77) * mm});
            skLineSegment(sketch, "E328", {"start": v(-10.1, -1.77) * mm, "end": v(-10.2, -1.94) * mm});
            skLineSegment(sketch, "E329", {"start": v(-10.2, -1.94) * mm, "end": v(-10.27, -2.14) * mm});
            skLineSegment(sketch, "E330", {"start": v(-10.27, -2.14) * mm, "end": v(-10.29, -2.34) * mm});
            skLineSegment(sketch, "E331", {"start": v(-10.29, -2.34) * mm, "end": v(-10.27, -2.54) * mm});
            skLineSegment(sketch, "E332", {"start": v(-10.27, -2.54) * mm, "end": v(-10.25, -2.59) * mm});
            skLineSegment(sketch, "E333", {"start": v(-10.25, -2.59) * mm, "end": v(-10.17, -2.78) * mm});
            skLineSegment(sketch, "E334", {"start": v(-10.17, -2.78) * mm, "end": v(-10.06, -2.94) * mm});
            skLineSegment(sketch, "E335", {"start": v(-10.06, -2.94) * mm, "end": v(-9.9, -3.08) * mm});
            skLineSegment(sketch, "E336", {"start": v(-9.9, -3.08) * mm, "end": v(-9.73, -3.18) * mm});
            skLineSegment(sketch, "E337", {"start": v(-9.73, -3.18) * mm, "end": v(-9.54, -3.24) * mm});
            skLineSegment(sketch, "E338", {"start": v(-9.54, -3.24) * mm, "end": v(-9.34, -3.26) * mm});
            skLineSegment(sketch, "E339", {"start": v(-9.34, -3.26) * mm, "end": v(-9.14, -3.24) * mm});
            skLineSegment(sketch, "E340", {"start": v(-9.14, -3.24) * mm, "end": v(-9.04, -3.2) * mm});
            skLineSegment(sketch, "E341", {"start": v(-9.04, -3.2) * mm, "end": v(-8.85, -3.13) * mm});
            skLineSegment(sketch, "E342", {"start": v(-8.85, -3.13) * mm, "end": v(-8.66, -3.05) * mm});
            skLineSegment(sketch, "E343", {"start": v(-8.66, -3.05) * mm, "end": v(-8.46, -2.96) * mm});
            skLineSegment(sketch, "E344", {"start": v(-8.46, -2.96) * mm, "end": v(-8.27, -2.88) * mm});
            skLineSegment(sketch, "E345", {"start": v(-8.27, -2.88) * mm, "end": v(-8.08, -2.8) * mm});
            skLineSegment(sketch, "E346", {"start": v(-8.08, -2.8) * mm, "end": v(-7.88, -2.72) * mm});
            skLineSegment(sketch, "E347", {"start": v(-7.88, -2.72) * mm, "end": v(-7.7, -2.64) * mm});
            skLineSegment(sketch, "E348", {"start": v(-7.7, -2.64) * mm, "end": v(-7.5, -2.56) * mm});
            skLineSegment(sketch, "E349", {"start": v(-7.5, -2.56) * mm, "end": v(-7.3, -2.48) * mm});
            skLineSegment(sketch, "E350", {"start": v(-7.3, -2.48) * mm, "end": v(-7.12, -2.4) * mm});
            skLineSegment(sketch, "E351", {"start": v(-7.12, -2.4) * mm, "end": v(-6.93, -2.32) * mm});
            skLineSegment(sketch, "E352", {"start": v(-6.93, -2.32) * mm, "end": v(-6.73, -2.23) * mm});
            skLineSegment(sketch, "E353", {"start": v(-6.73, -2.23) * mm, "end": v(-6.56, -2.16) * mm});
            skLineSegment(sketch, "E354", {"start": v(-6.56, -2.16) * mm, "end": v(-6.45, -2.34) * mm});
            skLineSegment(sketch, "E355", {"start": v(-6.45, -2.34) * mm, "end": v(-6.34, -2.51) * mm});
            skLineSegment(sketch, "E356", {"start": v(-6.34, -2.51) * mm, "end": v(-6.23, -2.68) * mm});
            skLineSegment(sketch, "E357", {"start": v(-6.23, -2.68) * mm, "end": v(-6.12, -2.86) * mm});
            skLineSegment(sketch, "E358", {"start": v(-6.12, -2.86) * mm, "end": v(-6, -3.03) * mm});
            skLineSegment(sketch, "E359", {"start": v(-6, -3.03) * mm, "end": v(-5.9, -3.2) * mm});
            skLineSegment(sketch, "E360", {"start": v(-5.9, -3.2) * mm, "end": v(-5.78, -3.38) * mm});
            skLineSegment(sketch, "E361", {"start": v(-5.78, -3.38) * mm, "end": v(-5.67, -3.55) * mm});
            skLineSegment(sketch, "E362", {"start": v(-5.67, -3.55) * mm, "end": v(-5.56, -3.73) * mm});
            skLineSegment(sketch, "E363", {"start": v(-5.56, -3.73) * mm, "end": v(-5.53, -3.77) * mm});
            skLineSegment(sketch, "E364", {"start": v(-5.53, -3.77) * mm, "end": v(-5.69, -3.9) * mm});
            skLineSegment(sketch, "E365", {"start": v(-5.69, -3.9) * mm, "end": v(-5.84, -4.04) * mm});
            skLineSegment(sketch, "E366", {"start": v(-5.84, -4.04) * mm, "end": v(-6, -4.19) * mm});
            skLineSegment(sketch, "E367", {"start": v(-6, -4.19) * mm, "end": v(-6.15, -4.33) * mm});
            skLineSegment(sketch, "E368", {"start": v(-6.15, -4.33) * mm, "end": v(-6.3, -4.47) * mm});
            skLineSegment(sketch, "E369", {"start": v(-6.3, -4.47) * mm, "end": v(-6.46, -4.61) * mm});
            skLineSegment(sketch, "E370", {"start": v(-6.46, -4.61) * mm, "end": v(-6.6, -4.75) * mm});
            skLineSegment(sketch, "E371", {"start": v(-6.6, -4.75) * mm, "end": v(-6.76, -4.9) * mm});
            skLineSegment(sketch, "E372", {"start": v(-6.76, -4.9) * mm, "end": v(-6.92, -5.04) * mm});
            skLineSegment(sketch, "E373", {"start": v(-6.92, -5.04) * mm, "end": v(-7.07, -5.18) * mm});
            skLineSegment(sketch, "E374", {"start": v(-7.07, -5.18) * mm, "end": v(-7.22, -5.32) * mm});
            skLineSegment(sketch, "E375", {"start": v(-7.22, -5.32) * mm, "end": v(-7.38, -5.46) * mm});
            skLineSegment(sketch, "E376", {"start": v(-7.38, -5.46) * mm, "end": v(-7.53, -5.6) * mm});
            skLineSegment(sketch, "E377", {"start": v(-7.53, -5.6) * mm, "end": v(-7.66, -5.79) * mm});
            skLineSegment(sketch, "E378", {"start": v(-7.66, -5.79) * mm, "end": v(-7.74, -5.97) * mm});
            skLineSegment(sketch, "E379", {"start": v(-7.74, -5.97) * mm, "end": v(-7.77, -6.17) * mm});
            skLineSegment(sketch, "E380", {"start": v(-7.77, -6.17) * mm, "end": v(-7.77, -6.38) * mm});
            skLineSegment(sketch, "E381", {"start": v(-7.77, -6.38) * mm, "end": v(-7.71, -6.57) * mm});
            skLineSegment(sketch, "E382", {"start": v(-7.71, -6.57) * mm, "end": v(-7.62, -6.75) * mm});
            skLineSegment(sketch, "E383", {"start": v(-7.62, -6.75) * mm, "end": v(-7.5, -6.9) * mm});
            skLineSegment(sketch, "E384", {"start": v(-7.5, -6.9) * mm, "end": v(-7.45, -6.94) * mm});
            skLineSegment(sketch, "E385", {"start": v(-7.45, -6.94) * mm, "end": v(-7.29, -7.06) * mm});
            skLineSegment(sketch, "E386", {"start": v(-7.29, -7.06) * mm, "end": v(-7.1, -7.14) * mm});
            skLineSegment(sketch, "E387", {"start": v(-7.1, -7.14) * mm, "end": v(-6.9, -7.17) * mm});
            skLineSegment(sketch, "E388", {"start": v(-6.9, -7.17) * mm, "end": v(-6.7, -7.16) * mm});
            skLineSegment(sketch, "E389", {"start": v(-6.7, -7.16) * mm, "end": v(-6.5, -7.1) * mm});
            skLineSegment(sketch, "E390", {"start": v(-6.5, -7.1) * mm, "end": v(-6.32, -7.01) * mm});
            skLineSegment(sketch, "E391", {"start": v(-6.32, -7.01) * mm, "end": v(-6.16, -6.88) * mm});
            skLineSegment(sketch, "E392", {"start": v(-6.16, -6.88) * mm, "end": v(-6.1, -6.8) * mm});
            skLineSegment(sketch, "E393", {"start": v(-6.1, -6.8) * mm, "end": v(-5.98, -6.64) * mm});
            skLineSegment(sketch, "E394", {"start": v(-5.98, -6.64) * mm, "end": v(-5.86, -6.47) * mm});
            skLineSegment(sketch, "E395", {"start": v(-5.86, -6.47) * mm, "end": v(-5.74, -6.3) * mm});
            skLineSegment(sketch, "E396", {"start": v(-5.74, -6.3) * mm, "end": v(-5.63, -6.12) * mm});
            skLineSegment(sketch, "E397", {"start": v(-5.63, -6.12) * mm, "end": v(-5.5, -5.95) * mm});
            skLineSegment(sketch, "E398", {"start": v(-5.5, -5.95) * mm, "end": v(-5.39, -5.77) * mm});
            skLineSegment(sketch, "E399", {"start": v(-5.39, -5.77) * mm, "end": v(-5.27, -5.6) * mm});
            skLineSegment(sketch, "E400", {"start": v(-5.27, -5.6) * mm, "end": v(-5.16, -5.43) * mm});
            skLineSegment(sketch, "E401", {"start": v(-5.16, -5.43) * mm, "end": v(-5.04, -5.26) * mm});
            skLineSegment(sketch, "E402", {"start": v(-5.04, -5.26) * mm, "end": v(-4.92, -5.09) * mm});
            skLineSegment(sketch, "E403", {"start": v(-4.92, -5.09) * mm, "end": v(-4.8, -4.92) * mm});
            skLineSegment(sketch, "E404", {"start": v(-4.8, -4.92) * mm, "end": v(-4.68, -4.74) * mm});
            skLineSegment(sketch, "E405", {"start": v(-4.68, -4.74) * mm, "end": v(-4.58, -4.6) * mm});
            skLineSegment(sketch, "E406", {"start": v(-4.58, -4.6) * mm, "end": v(-4.4, -4.68) * mm});
            skLineSegment(sketch, "E407", {"start": v(-4.4, -4.68) * mm, "end": v(-4.2, -4.76) * mm});
            skLineSegment(sketch, "E408", {"start": v(-4.2, -4.76) * mm, "end": v(-4.02, -4.85) * mm});
            skLineSegment(sketch, "E409", {"start": v(-4.02, -4.85) * mm, "end": v(-3.83, -4.94) * mm});
            skLineSegment(sketch, "E410", {"start": v(-3.83, -4.94) * mm, "end": v(-3.64, -5.02) * mm});
            skLineSegment(sketch, "E411", {"start": v(-3.64, -5.02) * mm, "end": v(-3.45, -5.1) * mm});
            skLineSegment(sketch, "E412", {"start": v(-3.45, -5.1) * mm, "end": v(-3.27, -5.2) * mm});
            skLineSegment(sketch, "E413", {"start": v(-3.27, -5.2) * mm, "end": v(-3.08, -5.28) * mm});
            skLineSegment(sketch, "E414", {"start": v(-3.08, -5.28) * mm, "end": v(-2.89, -5.36) * mm});
            skLineSegment(sketch, "E415", {"start": v(-2.89, -5.36) * mm, "end": v(-2.85, -5.38) * mm});
            skLineSegment(sketch, "E416", {"start": v(-2.85, -5.38) * mm, "end": v(-2.9, -5.58) * mm});
            skLineSegment(sketch, "E417", {"start": v(-2.9, -5.58) * mm, "end": v(-2.95, -5.78) * mm});
            skLineSegment(sketch, "E418", {"start": v(-2.95, -5.78) * mm, "end": v(-3, -5.99) * mm});
            skLineSegment(sketch, "E419", {"start": v(-3, -5.99) * mm, "end": v(-3.06, -6.19) * mm});
            skLineSegment(sketch, "E420", {"start": v(-3.06, -6.19) * mm, "end": v(-3.11, -6.39) * mm});
            skLineSegment(sketch, "E421", {"start": v(-3.11, -6.39) * mm, "end": v(-3.17, -6.6) * mm});
            skLineSegment(sketch, "E422", {"start": v(-3.17, -6.6) * mm, "end": v(-3.22, -6.8) * mm});
            skLineSegment(sketch, "E423", {"start": v(-3.22, -6.8) * mm, "end": v(-3.27, -7) * mm});
            skLineSegment(sketch, "E424", {"start": v(-3.27, -7) * mm, "end": v(-3.33, -7.2) * mm});
            skLineSegment(sketch, "E425", {"start": v(-3.33, -7.2) * mm, "end": v(-3.38, -7.4) * mm});
            skLineSegment(sketch, "E426", {"start": v(-3.38, -7.4) * mm, "end": v(-3.43, -7.6) * mm});
            skLineSegment(sketch, "E427", {"start": v(-3.43, -7.6) * mm, "end": v(-3.48, -7.8) * mm});
            skLineSegment(sketch, "E428", {"start": v(-3.48, -7.8) * mm, "end": v(-3.53, -8) * mm});
            skLineSegment(sketch, "E429", {"start": v(-3.53, -8) * mm, "end": v(-3.55, -8.23) * mm});
            skLineSegment(sketch, "E430", {"start": v(-3.55, -8.23) * mm, "end": v(-3.5, -8.43) * mm});
            skLineSegment(sketch, "E431", {"start": v(-3.5, -8.43) * mm, "end": v(-3.43, -8.62) * mm});
            skLineSegment(sketch, "E432", {"start": v(-3.43, -8.62) * mm, "end": v(-3.31, -8.79) * mm});
            skLineSegment(sketch, "E433", {"start": v(-3.31, -8.79) * mm, "end": v(-3.16, -8.92) * mm});
            skLineSegment(sketch, "E434", {"start": v(-3.16, -8.92) * mm, "end": v(-2.99, -9.02) * mm});
            skLineSegment(sketch, "E435", {"start": v(-2.99, -9.02) * mm, "end": v(-2.8, -9.09) * mm});
            skLineSegment(sketch, "E436", {"start": v(-2.8, -9.09) * mm, "end": v(-2.6, -9.1) * mm});
            skLineSegment(sketch, "E437", {"start": v(-2.6, -9.1) * mm, "end": v(-2.4, -9.08) * mm});
            skLineSegment(sketch, "E438", {"start": v(-2.4, -9.08) * mm, "end": v(-2.2, -9) * mm});
            skLineSegment(sketch, "E439", {"start": v(-2.2, -9) * mm, "end": v(-2.03, -8.9) * mm});
            skLineSegment(sketch, "E440", {"start": v(-2.03, -8.9) * mm, "end": v(-1.88, -8.76) * mm});
            skLineSegment(sketch, "E441", {"start": v(-1.88, -8.76) * mm, "end": v(-1.77, -8.59) * mm});
            skLineSegment(sketch, "E442", {"start": v(-1.77, -8.59) * mm, "end": v(-1.7, -8.4) * mm});
            skLineSegment(sketch, "E443", {"start": v(-1.7, -8.4) * mm, "end": v(-1.68, -8.25) * mm});
            skLineSegment(sketch, "E444", {"start": v(-1.68, -8.25) * mm, "end": v(-1.67, -8.04) * mm});
            skLineSegment(sketch, "E445", {"start": v(-1.67, -8.04) * mm, "end": v(-1.66, -7.83) * mm});
            skLineSegment(sketch, "E446", {"start": v(-1.66, -7.83) * mm, "end": v(-1.66, -7.62) * mm});
            skLineSegment(sketch, "E447", {"start": v(-1.66, -7.62) * mm, "end": v(-1.65, -7.41) * mm});
            skLineSegment(sketch, "E448", {"start": v(-1.65, -7.41) * mm, "end": v(-1.65, -7.2) * mm});
            skLineSegment(sketch, "E449", {"start": v(-1.65, -7.2) * mm, "end": v(-1.64, -7) * mm});
            skLineSegment(sketch, "E450", {"start": v(-1.64, -7) * mm, "end": v(-1.63, -6.79) * mm});
            skLineSegment(sketch, "E451", {"start": v(-1.63, -6.79) * mm, "end": v(-1.63, -6.58) * mm});
            skLineSegment(sketch, "E452", {"start": v(-1.63, -6.58) * mm, "end": v(-1.62, -6.37) * mm});
            skLineSegment(sketch, "E453", {"start": v(-1.62, -6.37) * mm, "end": v(-1.62, -6.16) * mm});
            skLineSegment(sketch, "E454", {"start": v(-1.62, -6.16) * mm, "end": v(-1.61, -5.95) * mm});
            skLineSegment(sketch, "E455", {"start": v(-1.61, -5.95) * mm, "end": v(-1.6, -5.74) * mm});
            skLineSegment(sketch, "E456", {"start": v(-1.6, -5.74) * mm, "end": v(-1.6, -5.56) * mm});
            skLineSegment(sketch, "E457", {"start": v(-1.6, -5.56) * mm, "end": v(-1.4, -5.53) * mm});
            skLineSegment(sketch, "E458", {"start": v(-1.4, -5.53) * mm, "end": v(-1.19, -5.5) * mm});
            skLineSegment(sketch, "E459", {"start": v(-1.19, -5.5) * mm, "end": v(-0.99, -5.47) * mm});
            skLineSegment(sketch, "E460", {"start": v(-0.99, -5.47) * mm, "end": v(-0.78, -5.44) * mm});
            skLineSegment(sketch, "E461", {"start": v(-0.78, -5.44) * mm, "end": v(-0.58, -5.42) * mm});
            skLineSegment(sketch, "E462", {"start": v(-0.58, -5.42) * mm, "end": v(-0.37, -5.39) * mm});
            skLineSegment(sketch, "E463", {"start": v(-0.37, -5.39) * mm, "end": v(-0.17, -5.36) * mm});
            skLineSegment(sketch, "E464", {"start": v(-0.17, -5.36) * mm, "end": v(0.04, -5.33) * mm});
            skLineSegment(sketch, "E465", {"start": v(0.04, -5.33) * mm, "end": v(0.24, -5.3) * mm});
            skLineSegment(sketch, "E466", {"start": v(0.24, -5.3) * mm, "end": v(0.29, -5.3) * mm});
            skLineSegment(sketch, "E467", {"start": v(0.29, -5.3) * mm, "end": v(0.35, -5.49) * mm});
            skLineSegment(sketch, "E468", {"start": v(0.35, -5.49) * mm, "end": v(0.41, -5.68) * mm});
            skLineSegment(sketch, "E469", {"start": v(0.41, -5.68) * mm, "end": v(0.48, -5.89) * mm});
            skLineSegment(sketch, "E470", {"start": v(0.48, -5.89) * mm, "end": v(0.54, -6.08) * mm});
            skLineSegment(sketch, "E471", {"start": v(0.54, -6.08) * mm, "end": v(0.6, -6.28) * mm});
            skLineSegment(sketch, "E472", {"start": v(0.6, -6.28) * mm, "end": v(0.67, -6.48) * mm});
            skLineSegment(sketch, "E473", {"start": v(0.67, -6.48) * mm, "end": v(0.74, -6.68) * mm});
            skLineSegment(sketch, "E474", {"start": v(0.74, -6.68) * mm, "end": v(0.8, -6.88) * mm});
            skLineSegment(sketch, "E475", {"start": v(0.8, -6.88) * mm, "end": v(0.87, -7.08) * mm});
            skLineSegment(sketch, "E476", {"start": v(0.87, -7.08) * mm, "end": v(0.93, -7.28) * mm});
            skLineSegment(sketch, "E477", {"start": v(0.93, -7.28) * mm, "end": v(1, -7.47) * mm});
            skLineSegment(sketch, "E478", {"start": v(1, -7.47) * mm, "end": v(1.06, -7.67) * mm});
            skLineSegment(sketch, "E479", {"start": v(1.06, -7.67) * mm, "end": v(1.13, -7.87) * mm});
            skLineSegment(sketch, "E480", {"start": v(1.13, -7.87) * mm, "end": v(1.24, -8.07) * mm});
            skLineSegment(sketch, "E481", {"start": v(1.24, -8.07) * mm, "end": v(1.38, -8.21) * mm});
            skLineSegment(sketch, "E482", {"start": v(1.38, -8.21) * mm, "end": v(1.55, -8.33) * mm});
            skLineSegment(sketch, "E483", {"start": v(1.55, -8.33) * mm, "end": v(1.73, -8.4) * mm});
            skLineSegment(sketch, "E484", {"start": v(1.73, -8.4) * mm, "end": v(1.93, -8.44) * mm});
            skLineSegment(sketch, "E485", {"start": v(1.93, -8.44) * mm, "end": v(2.14, -8.43) * mm});
            skLineSegment(sketch, "E486", {"start": v(2.14, -8.43) * mm, "end": v(2.33, -8.38) * mm});
            skLineSegment(sketch, "E487", {"start": v(2.33, -8.38) * mm, "end": v(2.38, -8.36) * mm});
            skLineSegment(sketch, "E488", {"start": v(2.38, -8.36) * mm, "end": v(2.55, -8.25) * mm});
            skLineSegment(sketch, "E489", {"start": v(2.55, -8.25) * mm, "end": v(2.7, -8.11) * mm});
            skLineSegment(sketch, "E490", {"start": v(2.7, -8.11) * mm, "end": v(2.82, -7.95) * mm});
            skLineSegment(sketch, "E491", {"start": v(2.82, -7.95) * mm, "end": v(2.9, -7.76) * mm});
            skLineSegment(sketch, "E492", {"start": v(2.9, -7.76) * mm, "end": v(2.93, -7.56) * mm});
            skLineSegment(sketch, "E493", {"start": v(2.93, -7.56) * mm, "end": v(2.92, -7.36) * mm});
            skLineSegment(sketch, "E494", {"start": v(2.92, -7.36) * mm, "end": v(2.86, -7.16) * mm});
            skLineSegment(sketch, "E495", {"start": v(2.86, -7.16) * mm, "end": v(2.82, -7.07) * mm});
            skLineSegment(sketch, "E496", {"start": v(2.82, -7.07) * mm, "end": v(2.71, -6.9) * mm});
            skLineSegment(sketch, "E497", {"start": v(2.71, -6.9) * mm, "end": v(2.6, -6.71) * mm});
            skLineSegment(sketch, "E498", {"start": v(2.6, -6.71) * mm, "end": v(2.5, -6.53) * mm});
            skLineSegment(sketch, "E499", {"start": v(2.5, -6.53) * mm, "end": v(2.39, -6.35) * mm});
            skLineSegment(sketch, "E500", {"start": v(2.39, -6.35) * mm, "end": v(2.28, -6.18) * mm});
            skLineSegment(sketch, "E501", {"start": v(2.28, -6.18) * mm, "end": v(2.17, -6) * mm});
            skLineSegment(sketch, "E502", {"start": v(2.17, -6) * mm, "end": v(2.07, -5.82) * mm});
            skLineSegment(sketch, "E503", {"start": v(2.07, -5.82) * mm, "end": v(1.96, -5.64) * mm});
            skLineSegment(sketch, "E504", {"start": v(1.96, -5.64) * mm, "end": v(1.85, -5.46) * mm});
            skLineSegment(sketch, "E505", {"start": v(1.85, -5.46) * mm, "end": v(1.74, -5.28) * mm});
            skLineSegment(sketch, "E506", {"start": v(1.74, -5.28) * mm, "end": v(1.64, -5.1) * mm});
            skLineSegment(sketch, "E507", {"start": v(1.64, -5.1) * mm, "end": v(1.53, -4.92) * mm});
            skLineSegment(sketch, "E508", {"start": v(1.53, -4.92) * mm, "end": v(1.43, -4.77) * mm});
            skLineSegment(sketch, "E509", {"start": v(1.43, -4.77) * mm, "end": v(1.6, -4.63) * mm});
            skLineSegment(sketch, "E510", {"start": v(1.6, -4.63) * mm, "end": v(1.75, -4.5) * mm});
            skLineSegment(sketch, "E511", {"start": v(1.75, -4.5) * mm, "end": v(1.9, -4.36) * mm});
            skLineSegment(sketch, "E512", {"start": v(1.9, -4.36) * mm, "end": v(2.06, -4.23) * mm});
            skLineSegment(sketch, "E513", {"start": v(2.06, -4.23) * mm, "end": v(2.21, -4.1) * mm});
            skLineSegment(sketch, "E514", {"start": v(2.21, -4.1) * mm, "end": v(2.37, -3.96) * mm});
            skLineSegment(sketch, "E515", {"start": v(2.37, -3.96) * mm, "end": v(2.53, -3.82) * mm});
            skLineSegment(sketch, "E516", {"start": v(2.53, -3.82) * mm, "end": v(2.68, -3.69) * mm});
            skLineSegment(sketch, "E517", {"start": v(2.68, -3.69) * mm, "end": v(2.84, -3.55) * mm});
            skLineSegment(sketch, "E518", {"start": v(2.84, -3.55) * mm, "end": v(2.87, -3.52) * mm});
            skLineSegment(sketch, "E519", {"start": v(2.87, -3.52) * mm, "end": v(3.03, -3.65) * mm});
            skLineSegment(sketch, "E520", {"start": v(3.03, -3.65) * mm, "end": v(3.2, -3.78) * mm});
            skLineSegment(sketch, "E521", {"start": v(3.2, -3.78) * mm, "end": v(3.36, -3.92) * mm});
            skLineSegment(sketch, "E522", {"start": v(3.36, -3.92) * mm, "end": v(3.52, -4.05) * mm});
            skLineSegment(sketch, "E523", {"start": v(3.52, -4.05) * mm, "end": v(3.68, -4.18) * mm});
            skLineSegment(sketch, "E524", {"start": v(3.68, -4.18) * mm, "end": v(3.84, -4.31) * mm});
            skLineSegment(sketch, "E525", {"start": v(3.84, -4.31) * mm, "end": v(4, -4.44) * mm});
            skLineSegment(sketch, "E526", {"start": v(4, -4.44) * mm, "end": v(4.16, -4.57) * mm});
            skLineSegment(sketch, "E527", {"start": v(4.16, -4.57) * mm, "end": v(4.33, -4.7) * mm});
            skLineSegment(sketch, "E528", {"start": v(4.33, -4.7) * mm, "end": v(4.49, -4.84) * mm});
            skLineSegment(sketch, "E529", {"start": v(4.49, -4.84) * mm, "end": v(4.65, -4.97) * mm});
            skLineSegment(sketch, "E530", {"start": v(4.65, -4.97) * mm, "end": v(4.81, -5.1) * mm});
            skLineSegment(sketch, "E531", {"start": v(4.81, -5.1) * mm, "end": v(4.98, -5.23) * mm});
            skLineSegment(sketch, "E532", {"start": v(4.98, -5.23) * mm, "end": v(5.18, -5.34) * mm});
            skLineSegment(sketch, "E533", {"start": v(5.18, -5.34) * mm, "end": v(5.37, -5.39) * mm});
            skLineSegment(sketch, "E534", {"start": v(5.37, -5.39) * mm, "end": v(5.58, -5.4) * mm});
            skLineSegment(sketch, "E535", {"start": v(5.58, -5.4) * mm, "end": v(5.78, -5.36) * mm});
            skLineSegment(sketch, "E536", {"start": v(5.78, -5.36) * mm, "end": v(5.96, -5.28) * mm});
            skLineSegment(sketch, "E537", {"start": v(5.96, -5.28) * mm, "end": v(6.13, -5.16) * mm});
            skLineSegment(sketch, "E538", {"start": v(6.13, -5.16) * mm, "end": v(6.26, -5) * mm});
            skLineSegment(sketch, "E539", {"start": v(6.26, -5) * mm, "end": v(6.3, -4.97) * mm});
            skLineSegment(sketch, "E540", {"start": v(6.3, -4.97) * mm, "end": v(6.38, -4.79) * mm});
            skLineSegment(sketch, "E541", {"start": v(6.38, -4.79) * mm, "end": v(6.43, -4.59) * mm});
            skLineSegment(sketch, "E542", {"start": v(6.43, -4.59) * mm, "end": v(6.44, -4.39) * mm});
            skLineSegment(sketch, "E543", {"start": v(6.44, -4.39) * mm, "end": v(6.4, -4.19) * mm});
            skLineSegment(sketch, "E544", {"start": v(6.4, -4.19) * mm, "end": v(6.32, -4) * mm});
            skLineSegment(sketch, "E545", {"start": v(6.32, -4) * mm, "end": v(6.2, -3.83) * mm});
            skLineSegment(sketch, "E546", {"start": v(6.2, -3.83) * mm, "end": v(6.05, -3.7) * mm});
            skLineSegment(sketch, "E547", {"start": v(6.05, -3.7) * mm, "end": v(5.96, -3.64) * mm});
            skLineSegment(sketch, "E548", {"start": v(5.96, -3.64) * mm, "end": v(5.78, -3.55) * mm});
            skLineSegment(sketch, "E549", {"start": v(5.78, -3.55) * mm, "end": v(5.6, -3.46) * mm});
            skLineSegment(sketch, "E550", {"start": v(5.6, -3.46) * mm, "end": v(5.4, -3.37) * mm});
            skLineSegment(sketch, "E551", {"start": v(5.4, -3.37) * mm, "end": v(5.22, -3.28) * mm});
            skLineSegment(sketch, "E552", {"start": v(5.22, -3.28) * mm, "end": v(5.03, -3.18) * mm});
            skLineSegment(sketch, "E553", {"start": v(5.03, -3.18) * mm, "end": v(4.84, -3.1) * mm});
            skLineSegment(sketch, "E554", {"start": v(4.84, -3.1) * mm, "end": v(4.66, -3) * mm});
            skLineSegment(sketch, "E555", {"start": v(4.66, -3) * mm, "end": v(4.47, -2.9) * mm});
            skLineSegment(sketch, "E556", {"start": v(4.47, -2.9) * mm, "end": v(4.28, -2.81) * mm});
            skLineSegment(sketch, "E557", {"start": v(4.28, -2.81) * mm, "end": v(4.1, -2.72) * mm});
            skLineSegment(sketch, "E558", {"start": v(4.1, -2.72) * mm, "end": v(3.9, -2.63) * mm});
            skLineSegment(sketch, "E559", {"start": v(3.9, -2.63) * mm, "end": v(3.72, -2.54) * mm});
            skLineSegment(sketch, "E560", {"start": v(3.72, -2.54) * mm, "end": v(3.56, -2.46) * mm});
            skLineSegment(sketch, "E561", {"start": v(3.56, -2.46) * mm, "end": v(3.61, -2.26) * mm});
            skLineSegment(sketch, "E562", {"start": v(3.61, -2.26) * mm, "end": v(3.67, -2.06) * mm});
            skLineSegment(sketch, "E563", {"start": v(3.67, -2.06) * mm, "end": v(3.73, -1.86) * mm});
            skLineSegment(sketch, "E564", {"start": v(3.73, -1.86) * mm, "end": v(3.79, -1.67) * mm});
            skLineSegment(sketch, "E565", {"start": v(3.79, -1.67) * mm, "end": v(3.85, -1.47) * mm});
            skLineSegment(sketch, "E566", {"start": v(3.85, -1.47) * mm, "end": v(3.9, -1.27) * mm});
            skLineSegment(sketch, "E567", {"start": v(3.9, -1.27) * mm, "end": v(3.96, -1.07) * mm});
            skLineSegment(sketch, "E568", {"start": v(3.96, -1.07) * mm, "end": v(4.02, -0.87) * mm});
            skLineSegment(sketch, "E569", {"start": v(4.02, -0.87) * mm, "end": v(4.08, -0.67) * mm});
            skLineSegment(sketch, "E570", {"start": v(4.08, -0.67) * mm, "end": v(4.1, -0.63) * mm});
            skPoint(sketch, "E571", {"position": v(-1.44, 0) * mm});
            skCircle(sketch, "E572", {"center": v(-1.44, 0) * mm, "radius": 1.5 * mm});
            skLineSegment(sketch, "E573", {"start": v(-1.44, 1.5) * mm, "end": v(-1.44, -1) * mm, "construction": true});
            skLineSegment(sketch, "E574", {"start": v(-2.55, -1) * mm, "end": v(-0.32, -1) * mm});
            skSolve(sketch);
        }
        {
            var Q0;
            Q0=makeQuery(id+"F0.imprint","IMPRINT",FACE,{"disambiguationData":[TD([[makeQuery(id+"F0.imprint","IMPRINT",EDGE,{"derivedFrom":sQuery(id+"F0.wireOp",EDGE,"E0")}),1.0]])]});
            extrude(context, id + "F1", {"entities" : qUnion([Q0]), "depth" : 5 * mm});
        }
    });
